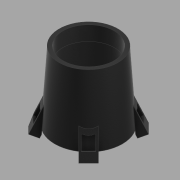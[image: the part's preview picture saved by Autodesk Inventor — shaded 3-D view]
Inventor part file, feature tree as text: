
AUTODESK INVENTOR PART (.ipt)
format: ipt  version: 2020 (Build 240168000, 168)  size: 798,208 bytes
history: native  units: mm
features: other x11, sketch x11, extrude x10, projected_geometry x4, plane x2, revolve x1, pattern_circular x1
ambient origin geometry x8: Origin, YZ Plane, XZ Plane, XY Plane, X Axis, Y Axis, Z Axis, Center Point
bodies: Solid1 (feature_tree), Solid2 (feature_tree), Solid3 (feature_tree), Solid4 (feature_tree), Solid5 (feature_tree), Solid6 (feature_tree)
feature tree (40):
  other  "Mounted Camera w Lens.iam"
  other  "Camera Mount 01.ipt:1"
  other  "Spinel USB Camera 01 trimmed.ipt:1"
  other  "M12 2.8-12mm F1.4 Lens.ipt:1"
  other  "WellTop"
  other  "CamYZ"
  other  "CamXY"
  other  "PipetteCutOff"
  other  "CamCenterLine"
  revolve  "Revolution1"  [1 undecoded]
  extrude  "Extrusion1"  Depth=35.71mm
  other  "LEDPlane"
  extrude  "Extrusion2"  Depth=30.0mm
  extrude  "Extrusion3"  TaperAngle=90.0deg  [1 undecoded]
  extrude  "Extrusion4"  Depth=10.0mm TaperAngle=0.0deg
  other  "Bend Part1"
  plane  "Work Plane6"
  sketch  "Sketch8"  dims[d19=50.0mm d20=50.0mm]
  extrude  "Extrusion6"  Depth=3.809229mm
  extrude  "Extrusion7"  Depth=2.65mm
  extrude  "Extrusion8"  Depth=50.0mm
  extrude  "Extrusion5"  Depth=1.5mm
  extrude  "Extrusion10"  Depth=50.0mm
  pattern_circular  "Circular Pattern1"  [2 undecoded]
  plane  "Work Plane7"
  extrude  "Extrusion9"  Depth=0.5mm
  sketch  "Sketch1"  dims[d0=10.0mm d1=40.0mm]
  sketch  "Sketch2"  dims[d4=17.65mm d5=35.71mm]
  sketch  "Sketch3"  dims[d6=8.0mm d7=30.0mm]
  sketch  "Sketch4"  dims[d8=2.5mm d9=90.0deg]
  sketch  "Sketch5"  dims[d10=1.5mm d11=10.0mm d12=0.0mm]
  projected_geometry  "Projected Loop1"
  sketch  "Sketch6"  dims[d13=8.586248mm d16=3.809229mm]
  sketch  "Sketch7"  dims[d17=3.809229mm d18=2.65mm]
  projected_geometry  "Projected Loop2"
  projected_geometry  "Projected Loop3"
  sketch  "Sketch9"  dims[d21=6.283185mm d22=1.5mm]
  sketch  "Sketch10"  dims[d23=3.490659mm d24=50.0mm]
  sketch  "Sketch11"  dims[d25=3.141593mm d26=3.0mm d27=3.490659mm d28=2.65mm d29=3.35mm d30=2.54mm d31=4.5mm d32=0.0mm d33=0.5mm d34=0.5mm d35=0.5mm d36=0.5mm d37=0.5mm d38=0.5mm d39=2.54mm d40=3.5mm d41=0.0mm d42=10.5mm d43=0.0mm d44=0.25mm d45=0.5mm d46=90.0deg d47=10.5mm d48=0.0mm d49=0.1mm d50=0.1mm d51=0.5mm d52=0.5mm d53=0.1mm d54=1.0mm d55=1.0mm d56=0.0mm d57=0.2mm d58=0.0mm d59=0.2mm d60=0.0mm d61=40.0mm d62=360.0deg d64=10.5mm d65=0.0mm d66=0.25mm d67=1.0mm d68=0.0mm d69=0.5mm d70=0.872665mm]
  projected_geometry  "Projected Loop4"
note: 4 required parameter values undecoded (feature->parameter linkage not recoverable at this tier; creation-order binding heuristic only, values carry confidence <= 0.55)